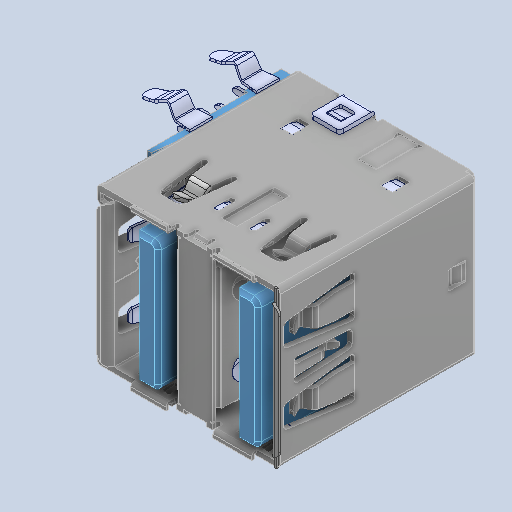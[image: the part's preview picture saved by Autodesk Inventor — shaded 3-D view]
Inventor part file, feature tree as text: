
AUTODESK INVENTOR PART (.ipt)
format: ipt  version: 2024.3 (Build 283343000, 343)  size: 1,667,072 bytes
history: native  units: in
note: dims shown in document units (in); Inventor stores cm internally (conversion verified against a paired STEP export)
features: chamfer x26, other x20, mirror x13, fillet x2
ambient origin geometry x8: Origin, YZ Plane, XZ Plane, XY Plane, X Axis, Y Axis, Z Axis, Center Point
bodies: Solid1 (feature_tree), Solid2 (feature_tree), Solid3 (feature_tree), Solid4 (feature_tree), Solid5 (feature_tree), Solid6 (feature_tree), Solid7 (feature_tree), Solid8 (feature_tree), Solid9 (feature_tree), Solid10 (feature_tree), Solid11 (feature_tree), Solid12 (feature_tree), Solid13 (feature_tree), Solid14 (feature_tree), Solid15 (feature_tree), Solid16 (feature_tree), Solid17 (feature_tree), Solid18 (feature_tree), Solid19 (feature_tree), Solid20 (feature_tree), Solid21 (feature_tree), Solid22 (feature_tree), Solid23 (feature_tree), Solid24 (feature_tree), Solid25 (feature_tree), Solid26 (feature_tree), Solid27 (feature_tree), Solid28 (feature_tree), Solid29 (feature_tree), Solid30 (feature_tree), Solid31 (feature_tree), Solid32 (feature_tree), Solid33 (feature_tree), Solid34 (feature_tree), Solid35 (feature_tree), Solid36 (feature_tree), Solid37 (feature_tree), Solid38 (feature_tree), Solid39 (feature_tree), Solid40 (feature_tree), Solid41 (feature_tree), Solid42 (feature_tree), Solid43 (feature_tree), Solid44 (feature_tree), Solid45 (feature_tree), Solid46 (feature_tree), Solid47 (feature_tree), Solid48 (feature_tree), Solid49 (feature_tree), Solid50 (feature_tree), Solid51 (feature_tree), Solid52 (feature_tree), Solid53 (feature_tree), Solid54 (feature_tree), Solid55 (feature_tree), Solid56 (feature_tree), Solid57 (feature_tree), Solid58 (feature_tree), Solid59 (feature_tree), Solid60 (feature_tree), Solid61 (feature_tree)
feature tree (61):
  chamfer  "Chamfer5"  [1 undecoded]
  chamfer  "Chamfer4"  [1 undecoded]
  other  "Boss-Extrude14"
  other  "LPattern1"
  mirror  "Mirror9[1]"
  mirror  "Mirror9[2]"
  other  "LPattern2[1]"
  other  "LPattern2[2]"
  other  "LPattern2[3]"
  other  "LPattern2[4]"
  other  "Cut-Extrude22"
  other  "Cut-Extrude23[1]"
  other  "Cut-Extrude23[2]"
  other  "Cut-Extrude23[3]"
  mirror  "Mirror18"
  other  "Cut-Extrude5[1]"
  other  "Cut-Extrude5[2]"
  other  "Cut-Extrude5[3]"
  chamfer  "Chamfer9"  [1 undecoded]
  chamfer  "Chamfer8"  [1 undecoded]
  fillet  "Fillet9"  [1 undecoded]
  chamfer  "Chamfer10"  [1 undecoded]
  other  "Cut-Extrude28"
  other  "Body-Move_Copy1[1]"
  other  "Body-Move_Copy1[2]"
  mirror  "Mirror19[1]"
  mirror  "Mirror19[2]"
  mirror  "Mirror19[3]"
  mirror  "Mirror19[4]"
  other  "Cut-Extrude31[1]"
  other  "Cut-Extrude31[2]"
  mirror  "Mirror23[1]"
  mirror  "Mirror23[2]"
  chamfer  "Chamfer15"  [1 undecoded]
  chamfer  "Chamfer14"  [1 undecoded]
  other  "Cut-Extrude34[1]"
  other  "Cut-Extrude34[2]"
  mirror  "Mirror27[1]"
  mirror  "Mirror27[2]"
  mirror  "Mirror29[1]"
  mirror  "Mirror29[2]"
  fillet  "Fillet13"  [1 undecoded]
  chamfer  "Chamfer31"  [1 undecoded]
  chamfer  "Chamfer36"  [1 undecoded]
  chamfer  "Chamfer35"  [1 undecoded]
  chamfer  "Chamfer34"  [1 undecoded]
  chamfer  "Chamfer33"  [1 undecoded]
  chamfer  "Chamfer22"  [1 undecoded]
  chamfer  "Chamfer21"  [1 undecoded]
  chamfer  "Chamfer20"  [1 undecoded]
  chamfer  "Chamfer19"  [1 undecoded]
  chamfer  "Chamfer23"  [1 undecoded]
  chamfer  "Chamfer24"  [1 undecoded]
  chamfer  "Chamfer25"  [1 undecoded]
  chamfer  "Chamfer26"  [1 undecoded]
  chamfer  "Chamfer27"  [1 undecoded]
  chamfer  "Chamfer28"  [1 undecoded]
  chamfer  "Chamfer29"  [1 undecoded]
  chamfer  "Chamfer30"  [1 undecoded]
  chamfer  "Chamfer32"  [1 undecoded]
  chamfer  "Chamfer38"  [1 undecoded]
note: 28 required parameter values undecoded (feature->parameter linkage not recoverable at this tier; creation-order binding heuristic only, values carry confidence <= 0.55)
